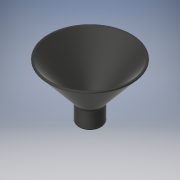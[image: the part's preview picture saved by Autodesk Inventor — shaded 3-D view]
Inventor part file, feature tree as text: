
AUTODESK INVENTOR PART (.ipt)
format: ipt  version: 2019 (Build 230136000, 136)  size: 157,184 bytes
history: native  units: mm
features: fillet x3, sketch x2, other x1
ambient origin geometry x8: Origin, YZ Plane, XZ Plane, XY Plane, X Axis, Y Axis, Z Axis, Center Point
bodies: Solide1 (feature_tree)
feature tree (6):
  sketch  "Esquisse 3D1"
  sketch  "Esquisse2"
  other  "Révolution1"
  fillet  "Congé1"  Radius=10.0mm
  fillet  "Congé2"  Radius=17.0mm
  fillet  "Congé3"  Radius=6.981317mm
